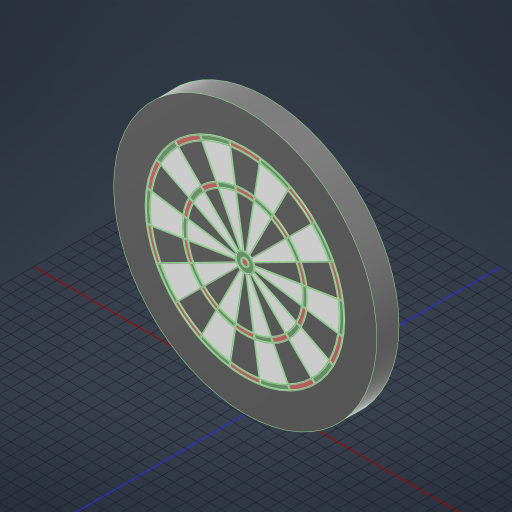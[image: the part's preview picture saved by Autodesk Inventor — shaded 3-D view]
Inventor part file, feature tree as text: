
AUTODESK INVENTOR PART (.ipt)
format: ipt  version: 2023.2 (Build 272271030, 271C)  size: 972,800 bytes
history: native  units: mm
features: extrude x9, pattern_circular x5, sketch x1
ambient origin geometry x8: Origin, YZ Plane, XZ Plane, XY Plane, X Axis, Y Axis, Z Axis, Center Point
bodies: Volumenkörper1 (feature_tree)
feature tree (15):
  sketch  "Skizze1"  dims[d1=450.9mm d2=340.0mm d3=8.0mm d4=8.0mm d5=12.7mm d6=31.89mm d7=214.0mm d8=1.570796mm d10=0.8mm d11=1.6mm d12=0.8mm d13=1.6mm d14=0.8mm d15=1.6mm d16=0.8mm d17=1.6mm d18=0.8mm d19=1.6mm d20=0.8mm d21=1.6mm d22=1.6mm d23=30.0mm d25=6.283185mm d27=38.0mm d28=0.0mm d29=38.0mm d30=0.0mm d36=38.0mm d37=0.0mm d38=38.0mm d39=0.0mm d40=39.0mm d41=0.0mm d42=100.0mm d43=360.0deg d45=100.0mm d46=360.0deg d48=100.0mm d49=360.0deg d51=100.0mm d52=360.0deg d54=200.0mm d55=360.0deg d57=38.0mm d58=0.0mm d59=38.0mm d60=0.0mm d61=39.0mm d62=0.0mm d63=38.0mm d64=0.0mm]
  extrude  "Extrusion1"  Depth=38.0mm
  extrude  "Extrusion2"  Depth=38.0mm
  extrude  "Extrusion4"  Depth=38.0mm
  extrude  "Extrusion5"  Depth=38.0mm
  extrude  "Extrusion6"  Depth=38.0mm
  extrude  "Extrusion7"  Depth=38.0mm
  extrude  "Extrusion8"  Depth=38.0mm
  extrude  "Extrusion9"  Depth=38.0mm
  pattern_circular  "Runde Anordnung2"  [2 undecoded]
  pattern_circular  "Runde Anordnung3"  [2 undecoded]
  pattern_circular  "Runde Anordnung4"  [2 undecoded]
  pattern_circular  "Runde Anordnung5"  [2 undecoded]
  pattern_circular  "Runde Anordnung6"  [2 undecoded]
  extrude  "Extrusion10"  Depth=38.0mm
note: 10 required parameter values undecoded (feature->parameter linkage not recoverable at this tier; creation-order binding heuristic only, values carry confidence <= 0.55)
